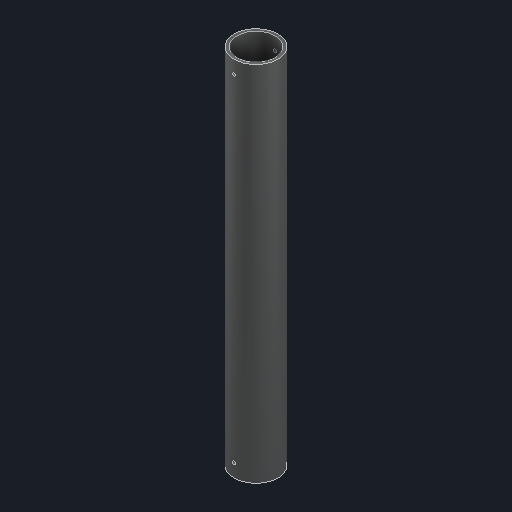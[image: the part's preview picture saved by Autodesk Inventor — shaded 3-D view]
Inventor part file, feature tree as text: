
AUTODESK INVENTOR PART (.ipt)
format: ipt  version: 2024 (Build 280153000, 153)  size: 106,496 bytes
history: native  units: in
note: dims shown in document units (in); Inventor stores cm internally (conversion verified against a paired STEP export)
features: mirror x1
ambient origin geometry x8: Origin, YZ Plane, XZ Plane, XY Plane, X Axis, Y Axis, Z Axis, Center Point
bodies: Solid1 (feature_tree)
feature tree (1):
  mirror  "Mirror1"
